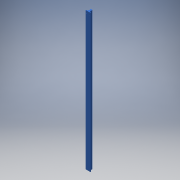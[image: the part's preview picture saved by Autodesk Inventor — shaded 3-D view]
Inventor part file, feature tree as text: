
AUTODESK INVENTOR PART (.ipt)
format: ipt  version: 2018 (Build 220112000, 112)  size: 141,312 bytes
history: native  units: mm
features: sketch x2, other x1, extrude x1, hole x1
ambient origin geometry x8: Origin, YZ Plane, XZ Plane, XY Plane, X Axis, Y Axis, Z Axis, Center Point
bodies: Body1 (feature_tree)
feature tree (5):
  other  "Sólido1"
  extrude  "Extrusão1"  Depth=25.0mm
  hole  "Furo1"  [1 undecoded]
  sketch  "Esboço1"  dims[d6=16.0mm d7=25.0mm]
  sketch  "Esboço3"  dims[d8=18.5mm d9=11.7mm d10=8.0mm d11=30.0deg d12=30.0deg d13=5.0mm d14=40.0mm d15=1200.0mm d16=0.0mm d18=15.0mm d19=15.0mm d20=5.5mm d21=5.5mm d22=20.0mm d28=5.5mm d29=6.0mm d30=4.0mm d31=2.0mm d32=90.0deg d33=8.0mm d34=20.594885mm]
note: 1 required parameter value undecoded (feature->parameter linkage not recoverable at this tier; creation-order binding heuristic only, values carry confidence <= 0.55)
